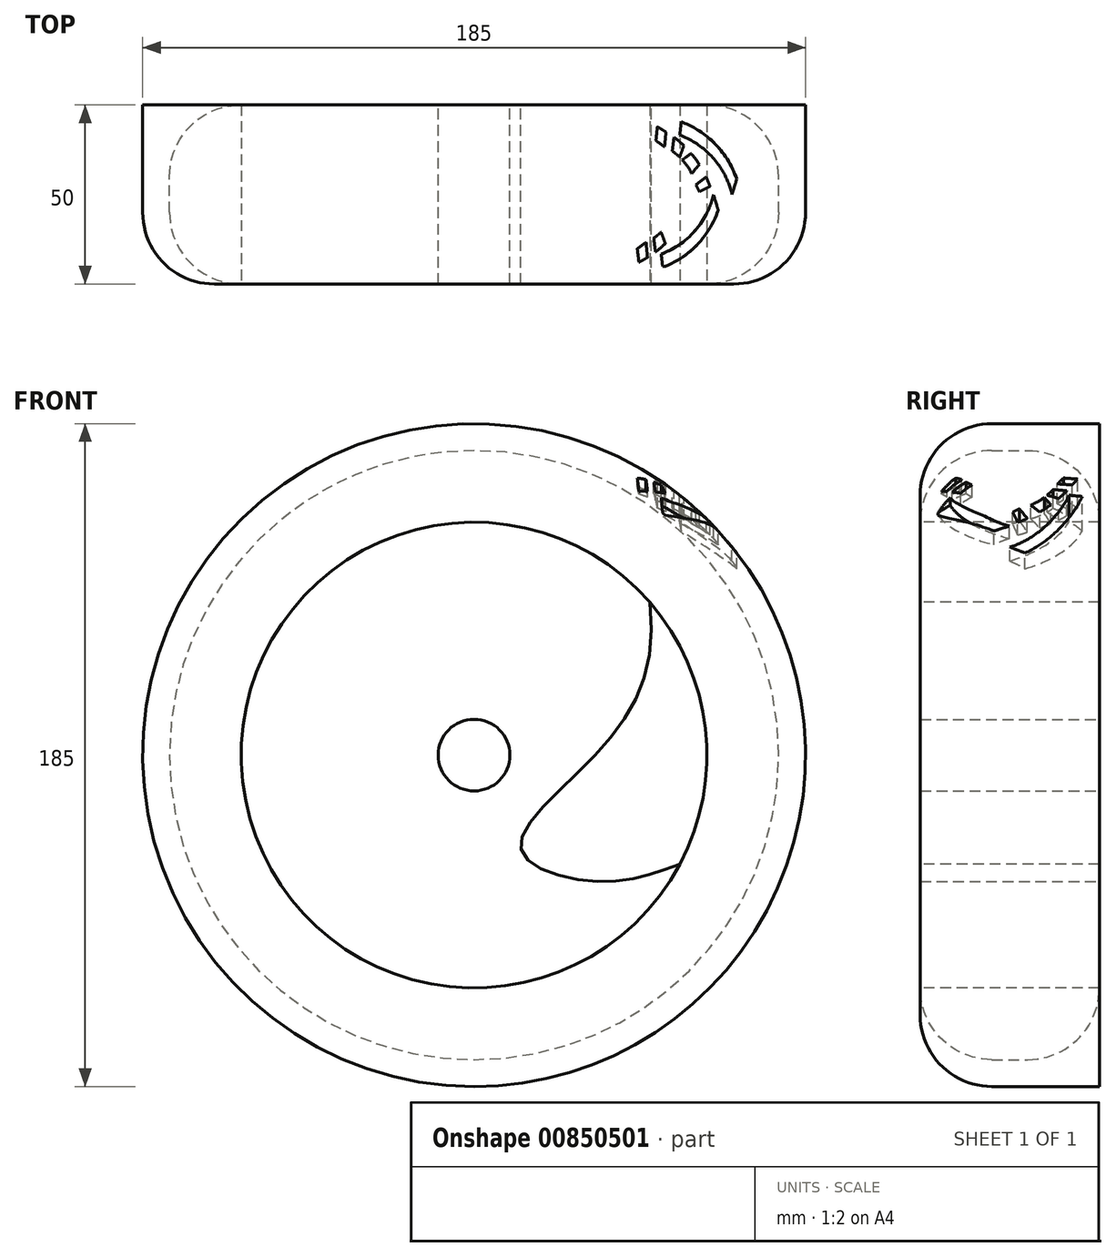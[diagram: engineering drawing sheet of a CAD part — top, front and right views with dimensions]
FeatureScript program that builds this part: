
annotation { "Feature Type Name" : "Feature", "Feature Type Description" : "" }
export const myFeature = defineFeature(function(context is Context, id is Id, definition is map)
    precondition{}
    {
        {
            var Q0;
            Q0=qCreatedBy(makeId("Front.planeOp"),FACE);
            var sketch = newSketch(context, id + "F0", { "sketchPlane" : qUnion([Q0])});
            skCircle(sketch, "E0", {"center": v(0, 0) * mm, "radius": 85 * mm});
            skCircle(sketch, "E1", {"center": v(0, 0) * mm, "radius": 10 * mm});
            skSolve(sketch);
        }
        {
            var Q0;
            Q0=makeQuery(id+"F0.imprint","IMPRINT",FACE,{"disambiguationData":[TD([[makeQuery(id+"F0.imprint","IMPRINT",EDGE,{"derivedFrom":sQuery(id+"F0.wireOp",EDGE,"E0")}),1.0]])]});
            extrude(context, id + "F1", {"entities" : qUnion([Q0]), "depth" : 25 * mm, "offsetDistance" : 25 * mm});
        }
        {
            var Q0;
            Q0=makeQuery(id+"F1.opExtrude","CAP_EDGE",EDGE,{"disambiguationData":[OSD([sQuery(id+"F0.wireOp",EDGE,"E0")])],"isStart":false});
            fillet(context, id + "F2", {"entities" : qUnion([Q0]), "radius" : 20 * mm, "tangentPropagation" : true, "allowEdgeOverflow" : false});
        }
        {
            var Q0;
            Q0=makeQuery(id+"F1.opExtrude","SWEPT_BODY",BODY,{"disambiguationData":[OSD([sQuery(id+"F0.wireOp",EDGE,"E0"),sQuery(id+"F0.wireOp",EDGE,"E1")])]});
            var Q1;
            Q1=makeQuery(id+"F1.opExtrude","CAP_FACE",FACE,{"disambiguationData":[OSD([sQuery(id+"F0.wireOp",EDGE,"E0"),sQuery(id+"F0.wireOp",EDGE,"E1")])],"isStart":true});
            mirror(context, id + "F3", {"operationType" : NewBodyOperationType.ADD, "entities" : qUnion([Q0]), "mirrorPlane" : qUnion([Q1])});
        }
        {
            var Q0;
            Q0=makeQuery(id+"F1.opExtrude","CAP_FACE",FACE,{"disambiguationData":[OSD([sQuery(id+"F0.wireOp",EDGE,"E0"),sQuery(id+"F0.wireOp",EDGE,"E1")])],"isStart":false});
            var sketch = newSketch(context, id + "F4", { "sketchPlane" : qUnion([Q0])});
            skFitSpline(sketch, "E2", {"points": [v(57.43, -30.45) * mm, v(34.18, -35.23) * mm, v(13.1, -26.2) * mm, v(33.73, 0) * mm, v(49.02, 42.7) * mm], "startDerivative": vector(-99.03, -36.57) * mm, "endDerivative": vector(-24, 187.35) * mm});
            skSolve(sketch);
        }
        {
            var Q0;
            {var subQ0=sQuery(id+"F4.wireOp",EDGE,"E2");Q0=makeQuery(id+"F4.imprint","IMPRINT",FACE,{"disambiguationData":[TD([[makeQuery(id+"F4.imprint","IMPRINT",EDGE,{"derivedFrom":subQ0}),-1.0]])]});}
            extrude(context, id + "F5", {"entities" : qUnion([Q0]), "operationType" : NewBodyOperationType.REMOVE, "oppositeDirection" : true, "depth" : 50 * mm, "offsetDistance" : 25 * mm});
        }
        {
            var Q0;
            Q0=makeQuery(id+"F1.opExtrude","CAP_FACE",FACE,{"disambiguationData":[OSD([sQuery(id+"F0.wireOp",EDGE,"E0"),sQuery(id+"F0.wireOp",EDGE,"E1")])],"isStart":false});
            var sketch = newSketch(context, id + "F6", { "sketchPlane" : qUnion([Q0])});
            skCircle(sketch, "E3", {"center": v(0, 0) * mm, "radius": 92.5 * mm});
            skCircle(sketch, "E4", {"center": v(0, 0) * mm, "radius": 85 * mm});
            skSolve(sketch);
        }
        {
            var Q0;
            Q0=makeQuery(id+"F6.imprint","IMPRINT",FACE,{"disambiguationData":[TD([[makeQuery(id+"F6.imprint","IMPRINT",EDGE,{"derivedFrom":sQuery(id+"F6.wireOp",EDGE,"E3")}),1.0]])]});
            var Q1;
            Q1=makeQuery(id+"F6.imprint","IMPRINT",FACE,{"disambiguationData":[TD([[makeQuery(id+"F6.imprint","IMPRINT",EDGE,{"derivedFrom":sQuery(id+"F6.wireOp",EDGE,"E4")}),1.0]])]});
            var Q2;
            Q2=makeQuery(id+"F3.opPattern","COPY",FACE,{"derivedFrom":makeQuery(id+"F1.opExtrude","CAP_FACE",FACE,{"disambiguationData":[OSD([sQuery(id+"F0.wireOp",EDGE,"E0"),sQuery(id+"F0.wireOp",EDGE,"E1")])],"isStart":false}),"instanceName":"1"});
            extrude(context, id + "F7", {"entities" : qUnion([Q0, Q1]), "endBound" : BoundingType.UP_TO_SURFACE, "oppositeDirection" : true, "depth" : 0 * mm, "endBoundEntityFace" : qUnion([Q2]), "offsetDistance" : 25 * mm});
        }
        {
            var Q0;
            Q0=makeQuery(id+"F7.opExtrude","CAP_EDGE",EDGE,{"disambiguationData":[OSD([sQuery(id+"F6.wireOp",EDGE,"E3")])],"isStart":true});
            var Q1;
            Q1=makeQuery(id+"F7.opExtrude","TWEAK_EDGE",EDGE,{"derivedFrom":[makeQuery(id+"F3.opPattern","COPY",FACE,{"derivedFrom":makeQuery(id+"F1.opExtrude","CAP_FACE",FACE,{"disambiguationData":[OSD([sQuery(id+"F0.wireOp",EDGE,"E0"),sQuery(id+"F0.wireOp",EDGE,"E1")])],"isStart":false}),"instanceName":"1"}),makeQuery(id+"F6.imprint","IMPRINT",EDGE,{"derivedFrom":sQuery(id+"F6.wireOp",EDGE,"E3")})]});
            fillet(context, id + "F8", {"entities" : qUnion([Q0, Q1]), "radius" : 20 * mm, "tangentPropagation" : true, "allowEdgeOverflow" : false});
        }
        {
            var Q0;
            Q0=qCreatedBy(makeId("Right.planeOp"),FACE);
            var sketch = newSketch(context, id + "F9", { "sketchPlane" : qUnion([Q0])});
            skArc(sketch, "E5", {"start": v(25.5, 82.1) * mm, "mid": v(0.07, 90.11) * mm, "end": v(-25.5, 82.59) * mm});
            skSolve(sketch);
        }
        {
            var Q0;
            Q0 = qSketchRegion(id + "F9", true);
            var Q1;
            Q1=sQuery(id+"F9.wireOp",EDGE,"E5");
            var Q2;
            Q2=makeQuery(id+"F3.opPattern","COPY",EDGE,{"derivedFrom":makeQuery(id+"F1.opExtrude","CAP_EDGE",EDGE,{"disambiguationData":[OSD([sQuery(id+"F0.wireOp",EDGE,"E1")])],"isStart":false}),"instanceName":"1"});
            revolve(context, id + "F10", {"bodyType" : ToolBodyType.SURFACE, "surfaceOperationType" : NewSurfaceOperationType.NEW, "entities" : qUnion([Q0]), "surfaceEntities" : qUnion([Q1]), "axis" : qUnion([Q2]), "revolveType" : RevolveType.FULL});
        }
        {
            var Q0;
            Q0=qCreatedBy(makeId("Top.planeOp"),FACE);
            cPlane(context, id + "F11", {"entities" : qUnion([Q0]), "cplaneType" : CPlaneType.OFFSET, "offset" : 92.5 * mm, "width" : 150 * mm, "height" : 150 * mm});
        }
        {
            var Q0;
            Q0=qCreatedBy(id+"F11.planeOp",FACE);
            var sketch = newSketch(context, id + "F12", { "sketchPlane" : qUnion([Q0])});
            skArc(sketch, "E6", {"start": v(72, 0) * mm, "mid": v(66.77, 10.1) * mm, "end": v(57.4, 16.56) * mm});
            skArc(sketch, "E7", {"start": v(73.3, 4.28) * mm, "mid": v(67.37, 14.01) * mm, "end": v(57.84, 20.26) * mm});
            skLineSegment(sketch, "E8", {"start": v(57.84, 20.26) * mm, "end": v(57.4, 16.56) * mm});
            skArc(sketch, "E9", {"start": v(65.83, 2.25) * mm, "mid": v(65.33, 3.58) * mm, "end": v(64.76, 4.9) * mm});
            skArc(sketch, "E10", {"start": v(60.74, 5.84) * mm, "mid": v(59.58, 7.84) * mm, "end": v(58.14, 9.65) * mm});
            skLineSegment(sketch, "E11", {"start": v(53.16, 13.3) * mm, "end": v(53.56, 17.45) * mm});
            skLineSegment(sketch, "E12", {"start": v(61.89, 2.68) * mm, "end": v(64.76, 4.9) * mm});
            skPoint(sketch, "E12.startSnap0", {"position": v(70.53, 2.68) * mm});
            skLineSegment(sketch, "E13", {"start": v(60.74, 5.84) * mm, "end": v(62.87, 8.37) * mm});
            skLineSegment(sketch, "E14", {"start": v(58.14, 9.65) * mm, "end": v(60.58, 11.46) * mm});
            skLineSegment(sketch, "E15", {"start": v(57.37, 10.43) * mm, "end": v(58.55, 13.62) * mm});
            skLineSegment(sketch, "E16", {"start": v(55.32, 12.07) * mm, "end": v(55.79, 15.96) * mm});
            skArc(sketch, "E17.trimOffspring", {"start": v(62.87, 8.37) * mm, "mid": v(61.78, 9.95) * mm, "end": v(60.58, 11.46) * mm});
            skLineSegment(sketch, "E18", {"start": v(65.83, 2.25) * mm, "end": v(62.9, 0.82) * mm});
            skLineSegment(sketch, "E19", {"start": v(62.9, 0.82) * mm, "end": v(61.89, 2.68) * mm});
            skArc(sketch, "E20.trimOffspring", {"start": v(57.37, 10.43) * mm, "mid": v(56.38, 11.3) * mm, "end": v(55.32, 12.07) * mm});
            skArc(sketch, "E21.trimOffspring", {"start": v(58.55, 13.62) * mm, "mid": v(57.2, 14.83) * mm, "end": v(55.79, 15.96) * mm});
            skLineSegment(sketch, "E22", {"start": v(53.56, 17.45) * mm, "end": v(51.18, 18.9) * mm});
            skLineSegment(sketch, "E23", {"start": v(51.18, 18.9) * mm, "end": v(50.73, 15.05) * mm});
            skLineSegment(sketch, "E24", {"start": v(50.73, 15.05) * mm, "end": v(53.16, 13.3) * mm});
            skLineSegment(sketch, "E25", {"start": v(72, 0) * mm, "end": v(73.3, 4.28) * mm});
            skArc(sketch, "E26.MirrorCS", {"start": v(60.66, -2.34) * mm, "mid": v(60.16, -3.67) * mm, "end": v(59.6, -4.98) * mm});
            skLineSegment(sketch, "E27.MirrorCS", {"start": v(56.72, -2.77) * mm, "end": v(59.6, -4.98) * mm});
            skLineSegment(sketch, "E28.MirrorCS", {"start": v(60.66, -2.34) * mm, "end": v(57.72, -0.9) * mm});
            skLineSegment(sketch, "E29.MirrorCS", {"start": v(57.72, -0.9) * mm, "end": v(56.72, -2.77) * mm});
            skLineSegment(sketch, "E30.MirrorCS", {"start": v(66.83, -0.09) * mm, "end": v(68.13, -4.37) * mm});
            skArc(sketch, "E31.MirrorCS", {"start": v(66.83, -0.09) * mm, "mid": v(61.6, -10.2) * mm, "end": v(52.22, -16.65) * mm});
            skArc(sketch, "E32.MirrorCS", {"start": v(68.13, -4.37) * mm, "mid": v(62.2, -14.1) * mm, "end": v(52.67, -20.35) * mm});
            skLineSegment(sketch, "E33.MirrorCS", {"start": v(52.67, -20.35) * mm, "end": v(52.22, -16.65) * mm});
            skArc(sketch, "E34.MirrorCS", {"start": v(57.7, -8.46) * mm, "mid": v(56.6, -10.04) * mm, "end": v(55.41, -11.55) * mm});
            skArc(sketch, "E35.MirrorCS", {"start": v(55.57, -5.93) * mm, "mid": v(54.41, -7.93) * mm, "end": v(52.97, -9.74) * mm});
            skLineSegment(sketch, "E36.MirrorCS", {"start": v(55.57, -5.93) * mm, "end": v(57.7, -8.46) * mm});
            skLineSegment(sketch, "E37.MirrorCS", {"start": v(52.97, -9.74) * mm, "end": v(55.41, -11.55) * mm});
            skLineSegment(sketch, "E38.MirrorCS", {"start": v(52.2, -10.52) * mm, "end": v(53.38, -13.7) * mm});
            skLineSegment(sketch, "E39.MirrorCS", {"start": v(50.15, -12.16) * mm, "end": v(50.61, -16.04) * mm});
            skArc(sketch, "E40.MirrorCS", {"start": v(53.38, -13.7) * mm, "mid": v(52.03, -14.92) * mm, "end": v(50.61, -16.04) * mm});
            skArc(sketch, "E41.MirrorCS", {"start": v(52.2, -10.52) * mm, "mid": v(51.2, -11.38) * mm, "end": v(50.15, -12.16) * mm});
            skLineSegment(sketch, "E42.MirrorCS", {"start": v(45.56, -15.14) * mm, "end": v(47.99, -13.38) * mm});
            skLineSegment(sketch, "E43.MirrorCS", {"start": v(48.4, -17.54) * mm, "end": v(46, -18.98) * mm});
            skLineSegment(sketch, "E44.MirrorCS", {"start": v(46, -18.98) * mm, "end": v(45.56, -15.14) * mm});
            skLineSegment(sketch, "E45.MirrorCS", {"start": v(47.99, -13.38) * mm, "end": v(48.4, -17.54) * mm});
            skSolve(sketch);
        }
        {
            var Q0;
            Q0=makeQuery(id+"F12.imprint","IMPRINT",FACE,{"disambiguationData":[TD([[makeQuery(id+"F12.imprint","IMPRINT",EDGE,{"derivedFrom":sQuery(id+"F12.wireOp",EDGE,"E6")}),-1.0]])]});
            var Q1;
            Q1=makeQuery(id+"F12.imprint","IMPRINT",FACE,{"disambiguationData":[TD([[makeQuery(id+"F12.imprint","IMPRINT",EDGE,{"derivedFrom":sQuery(id+"F12.wireOp",EDGE,"E9")}),1.0]])]});
            var Q2;
            Q2=makeQuery(id+"F12.imprint","IMPRINT",FACE,{"disambiguationData":[TD([[makeQuery(id+"F12.imprint","IMPRINT",EDGE,{"derivedFrom":sQuery(id+"F12.wireOp",EDGE,"E10")}),-1.0]])]});
            var Q3;
            Q3=makeQuery(id+"F12.imprint","IMPRINT",FACE,{"disambiguationData":[TD([[makeQuery(id+"F12.imprint","IMPRINT",EDGE,{"derivedFrom":sQuery(id+"F12.wireOp",EDGE,"E15")}),1.0]])]});
            var Q4;
            Q4=makeQuery(id+"F12.imprint","IMPRINT",FACE,{"disambiguationData":[TD([[makeQuery(id+"F12.imprint","IMPRINT",EDGE,{"derivedFrom":sQuery(id+"F12.wireOp",EDGE,"E11")}),1.0]])]});
            var Q5;
            Q5=makeQuery(id+"F12.imprint","IMPRINT",FACE,{"disambiguationData":[TD([[makeQuery(id+"F12.imprint","IMPRINT",EDGE,{"derivedFrom":sQuery(id+"F12.wireOp",EDGE,"E30.MirrorCS")}),-1.0]])]});
            var Q6;
            Q6=makeQuery(id+"F12.imprint","IMPRINT",FACE,{"disambiguationData":[TD([[makeQuery(id+"F12.imprint","IMPRINT",EDGE,{"derivedFrom":sQuery(id+"F12.wireOp",EDGE,"E26.MirrorCS")}),-1.0]])]});
            var Q7;
            Q7=makeQuery(id+"F12.imprint","IMPRINT",FACE,{"disambiguationData":[TD([[makeQuery(id+"F12.imprint","IMPRINT",EDGE,{"derivedFrom":sQuery(id+"F12.wireOp",EDGE,"E34.MirrorCS")}),-1.0]])]});
            var Q8;
            Q8=makeQuery(id+"F12.imprint","IMPRINT",FACE,{"disambiguationData":[TD([[makeQuery(id+"F12.imprint","IMPRINT",EDGE,{"derivedFrom":sQuery(id+"F12.wireOp",EDGE,"E38.MirrorCS")}),-1.0]])]});
            var Q9;
            Q9=makeQuery(id+"F12.imprint","IMPRINT",FACE,{"disambiguationData":[TD([[makeQuery(id+"F12.imprint","IMPRINT",EDGE,{"derivedFrom":sQuery(id+"F12.wireOp",EDGE,"E42.MirrorCS")}),-1.0]])]});
            var Q10;
            Q10=makeQuery(id+"F10.opRevolve","SWEPT_FACE",FACE,{"disambiguationData":[OSD([sQuery(id+"F9.wireOp",EDGE,"E5")])]});
            extrude(context, id + "F13", {"entities" : qUnion([Q0, Q1, Q2, Q3, Q4, Q5, Q6, Q7, Q8, Q9]), "operationType" : NewBodyOperationType.REMOVE, "endBound" : BoundingType.UP_TO_SURFACE, "oppositeDirection" : true, "depth" : 25 * mm, "endBoundEntityFace" : qUnion([Q10]), "offsetDistance" : 25 * mm});
        }
    });
